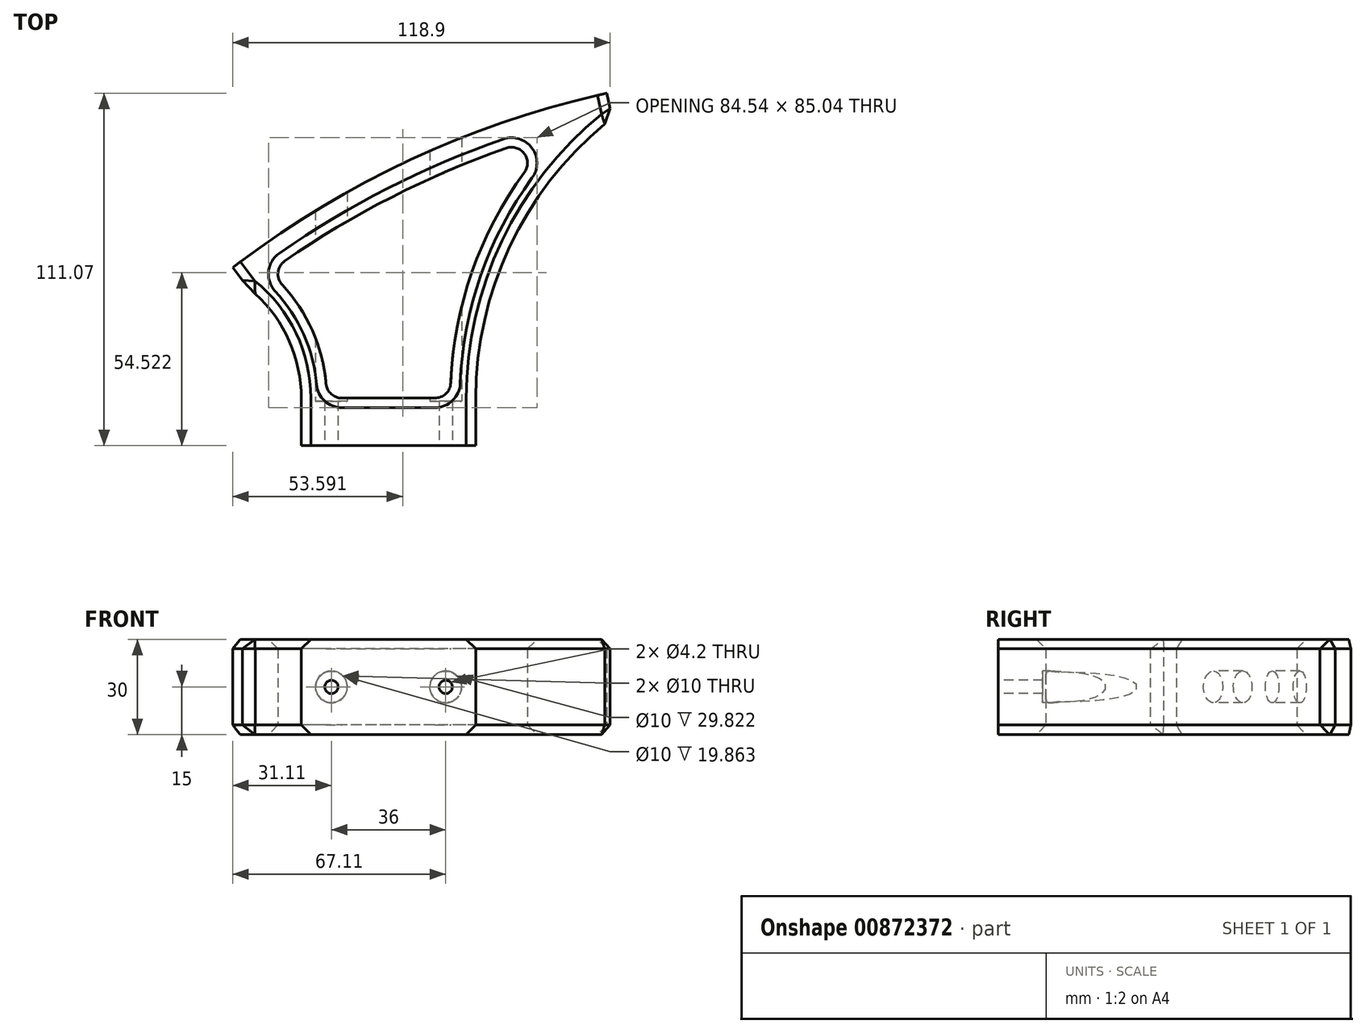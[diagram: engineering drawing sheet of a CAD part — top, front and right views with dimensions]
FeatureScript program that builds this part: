
annotation { "Feature Type Name" : "Feature", "Feature Type Description" : "" }
export const myFeature = defineFeature(function(context is Context, id is Id, definition is map)
    precondition{}
    {
        {
            var Q0;
            Q0=qCreatedBy(makeId("Top.planeOp"),FACE);
            var sketch = newSketch(context, id + "F0", { "sketchPlane" : qUnion([Q0])});
            skLineSegment(sketch, "E0", {"start": v(0, 0) * mm, "end": v(120, 55.96) * mm, "construction": true});
            skLineSegment(sketch, "E1", {"start": v(0, 0) * mm, "end": v(55, 0) * mm, "construction": true});
            skLineSegment(sketch, "E2", {"start": v(55, 0) * mm, "end": v(55, 25.65) * mm, "construction": true});
            skLineSegment(sketch, "E3", {"start": v(97.94, 103.26) * mm, "end": v(120, 55.96) * mm, "construction": true});
            skLineSegment(sketch, "E4", {"start": v(0, 0) * mm, "end": v(55, 0) * mm});
            skLineSegment(sketch, "E5", {"start": v(-21.6, 56.13) * mm, "end": v(96.21, 111.07) * mm, "construction": true});
            skLineSegment(sketch, "E6", {"start": v(0, 0) * mm, "end": v(0, 15) * mm});
            skLineSegment(sketch, "E7", {"start": v(0, 15) * mm, "end": v(55, 15) * mm, "construction": true});
            skArc(sketch, "E8", {"start": v(70.28, 86.09) * mm, "mid": v(53.74, 54.68) * mm, "end": v(47.1, 19.8) * mm});
            skArc(sketch, "E9.filletArc", {"start": v(42.1, 15) * mm, "mid": v(45.56, 16.4) * mm, "end": v(47.1, 19.8) * mm});
            skLineSegment(sketch, "E10", {"start": v(37.3, 83.6) * mm, "end": v(161.08, -181.84) * mm, "construction": true});
            skArc(sketch, "E11", {"start": v(-21.6, 56.13) * mm, "mid": v(34.3, 90.06) * mm, "end": v(96.21, 111.07) * mm});
            skLineSegment(sketch, "E12", {"start": v(97.94, 103.26) * mm, "end": v(96.21, 111.07) * mm});
            skLineSegment(sketch, "E13", {"start": v(-21.6, 56.13) * mm, "end": v(-16.73, 49.78) * mm});
            skArc(sketch, "E14", {"start": v(97.94, 103.26) * mm, "mid": v(37.67, 82.8) * mm, "end": v(-16.73, 49.78) * mm, "construction": true});
            skArc(sketch, "E15", {"start": v(0, 15) * mm, "mid": v(-4.4, 34.3) * mm, "end": v(-16.73, 49.78) * mm});
            skArc(sketch, "E16", {"start": v(97.94, 103.26) * mm, "mid": v(66.3, 64.08) * mm, "end": v(55, 15) * mm});
            skLineSegment(sketch, "E17", {"start": v(55, 15) * mm, "end": v(55, 0) * mm});
            skLineSegment(sketch, "E18", {"start": v(12.78, 15) * mm, "end": v(42.1, 15) * mm});
            skArc(sketch, "E19", {"start": v(70.28, 86.09) * mm, "mid": v(70.27, 92.02) * mm, "end": v(64.6, 93.77) * mm});
            skArc(sketch, "E20", {"start": v(64.6, 93.77) * mm, "mid": v(28.51, 78.34) * mm, "end": v(-5.18, 58.2) * mm});
            skArc(sketch, "E21", {"start": v(7.8, 19.57) * mm, "mid": v(3.5, 36.28) * mm, "end": v(-6, 50.7) * mm});
            skArc(sketch, "E22", {"start": v(-5.18, 58.2) * mm, "mid": v(-7.3, 54.64) * mm, "end": v(-6, 50.7) * mm});
            skArc(sketch, "E23", {"start": v(7.8, 19.57) * mm, "mid": v(9.4, 16.31) * mm, "end": v(12.78, 15) * mm});
            skSolve(sketch);
        }
        {
            var Q0;
            Q0=makeQuery(id+"F0.imprint","IMPRINT",FACE,{"disambiguationData":[TD([[makeQuery(id+"F0.imprint","IMPRINT",EDGE,{"derivedFrom":sQuery(id+"F0.wireOp",EDGE,"E4")}),1.0]])]});
            extrude(context, id + "F1", {"entities" : qUnion([Q0]), "depth" : 30 * mm, "offsetDistance" : 25 * mm});
        }
        {
            var Q0;
            Q0=makeQuery(id+"F1.opExtrude","SWEPT_FACE",FACE,{"disambiguationData":[OSD([sQuery(id+"F0.wireOp",EDGE,"E4")])]});
            var sketch = newSketch(context, id + "F2", { "sketchPlane" : qUnion([Q0])});
            skLineSegment(sketch, "E24", {"start": v(0, 15) * mm, "end": v(0, 15) * mm});
            skLineSegment(sketch, "E25", {"start": v(27.5, 30) * mm, "end": v(27.5, 0) * mm, "construction": true});
            skCircle(sketch, "E26", {"center": v(45.5, 15) * mm, "radius": 2.1 * mm});
            skCircle(sketch, "E27", {"center": v(9.5, 15) * mm, "radius": 2.1 * mm});
            skSolve(sketch);
        }
        {
            var Q0;
            Q0 = qSketchRegion(id + "F2", true);
            extrude(context, id + "F3", {"entities" : qUnion([Q0]), "operationType" : NewBodyOperationType.REMOVE, "endBound" : BoundingType.THROUGH_ALL, "oppositeDirection" : true, "depth" : 25 * mm, "offsetDistance" : 25 * mm});
        }
        {
            var Q0;
            Q0=makeQuery(id+"F1.opExtrude","SWEPT_FACE",FACE,{"disambiguationData":[OSD([sQuery(id+"F0.wireOp",EDGE,"E18")])]});
            var sketch = newSketch(context, id + "F4", { "sketchPlane" : qUnion([Q0])});
            skCircle(sketch, "E28", {"center": v(-45.5, 15) * mm, "radius": 5 * mm});
            skCircle(sketch, "E29", {"center": v(-9.5, 15) * mm, "radius": 5 * mm});
            skSolve(sketch);
        }
        {
            var Q0;
            Q0 = qSketchRegion(id + "F4", true);
            extrude(context, id + "F5", {"entities" : qUnion([Q0]), "operationType" : NewBodyOperationType.REMOVE, "endBound" : BoundingType.THROUGH_ALL, "depth" : 25 * mm, "offsetDistance" : 25 * mm, "hasSecondDirection" : true, "secondDirectionOppositeDirection" : true, "secondDirectionDepth" : 1 * mm});
        }
        {
            var Q0;
            Q0=makeQuery(id+"F1.opExtrude","CAP_EDGE",EDGE,{"disambiguationData":[OSD([sQuery(id+"F0.wireOp",EDGE,"E17")])],"isStart":true});
            var Q1;
            Q1=makeQuery(id+"F1.opExtrude","CAP_EDGE",EDGE,{"disambiguationData":[OSD([sQuery(id+"F0.wireOp",EDGE,"E17")])],"isStart":false});
            var Q2;
            Q2=makeQuery(id+"F1.opExtrude","CAP_EDGE",EDGE,{"disambiguationData":[OSD([sQuery(id+"F0.wireOp",EDGE,"E6")])],"isStart":true});
            var Q3;
            Q3=makeQuery(id+"F1.opExtrude","CAP_EDGE",EDGE,{"disambiguationData":[OSD([sQuery(id+"F0.wireOp",EDGE,"E6")])],"isStart":false});
            var Q4;
            Q4=makeQuery(id+"F1.opExtrude","CAP_EDGE",EDGE,{"disambiguationData":[OSD([sQuery(id+"F0.wireOp",EDGE,"E12")])],"isStart":true});
            var Q5;
            Q5=makeQuery(id+"F1.opExtrude","CAP_EDGE",EDGE,{"disambiguationData":[OSD([sQuery(id+"F0.wireOp",EDGE,"E13")])],"isStart":true});
            var Q6;
            Q6=makeQuery(id+"F1.opExtrude","CAP_EDGE",EDGE,{"disambiguationData":[OSD([sQuery(id+"F0.wireOp",EDGE,"E13")])],"isStart":false});
            var Q7;
            Q7=makeQuery(id+"F1.opExtrude","CAP_EDGE",EDGE,{"disambiguationData":[OSD([sQuery(id+"F0.wireOp",EDGE,"E12")])],"isStart":false});
            var Q8;
            Q8=makeQuery(id+"F1.opExtrude","CAP_EDGE",EDGE,{"disambiguationData":[OSD([sQuery(id+"F0.wireOp",EDGE,"E20")])],"isStart":false});
            var Q9;
            Q9=makeQuery(id+"F1.opExtrude","CAP_EDGE",EDGE,{"disambiguationData":[OSD([sQuery(id+"F0.wireOp",EDGE,"E20")])],"isStart":true});
            var Q10;
            Q10=makeQuery(id+"F1.opExtrude","SWEPT_EDGE",EDGE,{"disambiguationData":[OSD([sQuery(id+"F0.wireOp",EDGE,"E12"),sQuery(id+"F0.wireOp",EDGE,"E16")])]});
            var Q11;
            Q11=makeQuery(id+"F1.opExtrude","SWEPT_EDGE",EDGE,{"disambiguationData":[OSD([sQuery(id+"F0.wireOp",EDGE,"E13"),sQuery(id+"F0.wireOp",EDGE,"E15")])]});
            chamfer(context, id + "F6", {"entities" : qUnion([Q0, Q1, Q2, Q3, Q4, Q5, Q6, Q7, Q8, Q9, Q10, Q11]), "width" : 3 * mm, "tangentPropagation" : true});
        }
    });
